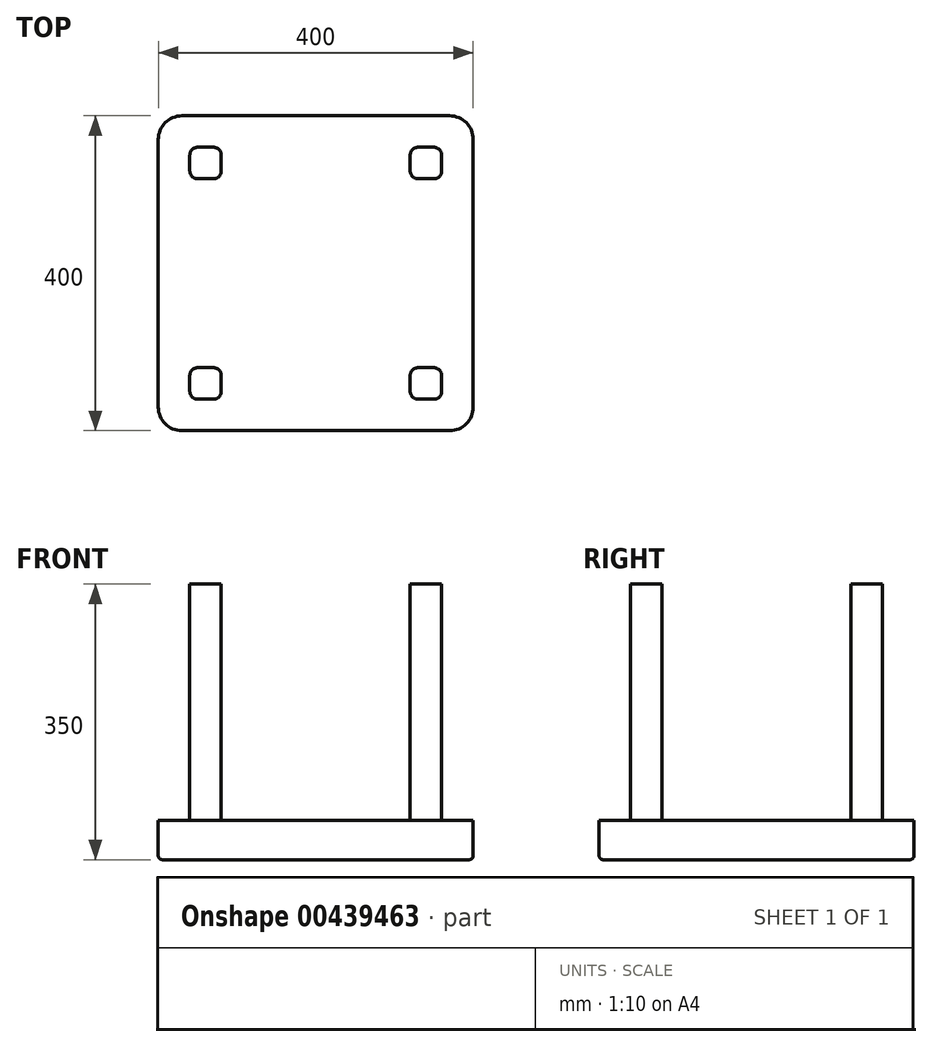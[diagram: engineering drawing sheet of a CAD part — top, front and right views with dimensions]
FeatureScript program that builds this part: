
annotation { "Feature Type Name" : "Feature", "Feature Type Description" : "" }
export const myFeature = defineFeature(function(context is Context, id is Id, definition is map)
    precondition{}
    {
        {
            var Q0;
            Q0=qCreatedBy(makeId("Top.planeOp"),FACE);
            var sketch = newSketch(context, id + "F0", { "sketchPlane" : qUnion([Q0])});
            skLineSegment(sketch, "E0.bottom", {"start": v(-186.1, 208.07) * mm, "end": v(153.9, 208.07) * mm});
            skLineSegment(sketch, "E0.top", {"start": v(-186.1, -191.93) * mm, "end": v(153.9, -191.93) * mm});
            skLineSegment(sketch, "E0.left", {"start": v(-216.1, 178.07) * mm, "end": v(-216.1, -161.93) * mm});
            skLineSegment(sketch, "E0.right", {"start": v(183.9, 178.07) * mm, "end": v(183.9, -161.93) * mm});
            skPoint(sketch, "E1.visualSharp", {"position": v(-216.1, 208.07) * mm});
            skArc(sketch, "E1.filletArc", {"start": v(-186.1, 208.07) * mm, "mid": v(-207.3, 199.28) * mm, "end": v(-216.1, 178.07) * mm});
            skPoint(sketch, "E2.visualSharp", {"position": v(183.9, 208.07) * mm});
            skArc(sketch, "E2.filletArc", {"start": v(183.9, 178.07) * mm, "mid": v(175.12, 199.28) * mm, "end": v(153.9, 208.07) * mm});
            skPoint(sketch, "E3.visualSharp", {"position": v(183.9, -191.93) * mm});
            skArc(sketch, "E3.filletArc", {"start": v(153.9, -191.93) * mm, "mid": v(175.12, -183.15) * mm, "end": v(183.9, -161.93) * mm});
            skPoint(sketch, "E4.visualSharp", {"position": v(-216.1, -191.93) * mm});
            skArc(sketch, "E4.filletArc", {"start": v(-216.1, -161.93) * mm, "mid": v(-207.3, -183.15) * mm, "end": v(-186.1, -191.93) * mm});
            skSolve(sketch);
        }
        {
            var Q0;
            Q0=makeQuery(id+"F0.imprint","IMPRINT",FACE,{"disambiguationData":[TD([[makeQuery(id+"F0.imprint","IMPRINT",EDGE,{"derivedFrom":sQuery(id+"F0.wireOp",EDGE,"E0.bottom")}),-1.0]])]});
            extrude(context, id + "F1", {"entities" : qUnion([Q0]), "depth" : 50 * mm});
        }
        {
            var Q0;
            Q0=qCreatedBy(makeId("Top.planeOp"),FACE);
            var sketch = newSketch(context, id + "F2", { "sketchPlane" : qUnion([Q0])});
            skLineSegment(sketch, "E5.bottom", {"start": v(133.9, -151.93) * mm, "end": v(113.9, -151.93) * mm});
            skLineSegment(sketch, "E5.top", {"start": v(133.9, -111.93) * mm, "end": v(113.9, -111.93) * mm});
            skLineSegment(sketch, "E5.left", {"start": v(143.9, -141.93) * mm, "end": v(143.9, -121.93) * mm});
            skLineSegment(sketch, "E5.right", {"start": v(103.9, -141.93) * mm, "end": v(103.9, -121.93) * mm});
            skLineSegment(sketch, "E6.bottom", {"start": v(133.9, 128.07) * mm, "end": v(113.9, 128.07) * mm});
            skLineSegment(sketch, "E6.top", {"start": v(133.9, 168.07) * mm, "end": v(113.9, 168.07) * mm});
            skLineSegment(sketch, "E6.left", {"start": v(143.9, 138.07) * mm, "end": v(143.9, 158.07) * mm});
            skLineSegment(sketch, "E6.right", {"start": v(103.9, 138.07) * mm, "end": v(103.9, 158.07) * mm});
            skLineSegment(sketch, "E7.bottom", {"start": v(-146.1, -151.93) * mm, "end": v(-166.1, -151.93) * mm});
            skLineSegment(sketch, "E7.top", {"start": v(-146.1, -111.93) * mm, "end": v(-166.1, -111.93) * mm});
            skLineSegment(sketch, "E7.left", {"start": v(-136.1, -141.93) * mm, "end": v(-136.1, -121.93) * mm});
            skLineSegment(sketch, "E7.right", {"start": v(-176.1, -141.93) * mm, "end": v(-176.1, -121.93) * mm});
            skLineSegment(sketch, "E8.bottom", {"start": v(-146.1, 128.07) * mm, "end": v(-166.1, 128.07) * mm});
            skLineSegment(sketch, "E8.top", {"start": v(-146.1, 168.07) * mm, "end": v(-166.1, 168.07) * mm});
            skLineSegment(sketch, "E8.left", {"start": v(-136.1, 138.07) * mm, "end": v(-136.1, 158.07) * mm});
            skLineSegment(sketch, "E8.right", {"start": v(-176.1, 138.07) * mm, "end": v(-176.1, 158.07) * mm});
            skPoint(sketch, "E9.visualSharp", {"position": v(-176.1, -151.93) * mm});
            skArc(sketch, "E9.filletArc", {"start": v(-176.1, -141.93) * mm, "mid": v(-173.16, -149) * mm, "end": v(-166.1, -151.93) * mm});
            skPoint(sketch, "E10.visualSharp", {"position": v(-176.1, -111.93) * mm});
            skArc(sketch, "E10.filletArc", {"start": v(-166.1, -111.93) * mm, "mid": v(-173.16, -114.86) * mm, "end": v(-176.1, -121.93) * mm});
            skPoint(sketch, "E11.visualSharp", {"position": v(-136.1, -111.93) * mm});
            skArc(sketch, "E11.filletArc", {"start": v(-136.1, -121.93) * mm, "mid": v(-139.02, -114.86) * mm, "end": v(-146.1, -111.93) * mm});
            skPoint(sketch, "E12.visualSharp", {"position": v(-136.1, -151.93) * mm});
            skArc(sketch, "E12.filletArc", {"start": v(-146.1, -151.93) * mm, "mid": v(-139.02, -149) * mm, "end": v(-136.1, -141.93) * mm});
            skPoint(sketch, "E13.visualSharp", {"position": v(-176.1, 128.07) * mm});
            skArc(sketch, "E13.filletArc", {"start": v(-176.1, 138.07) * mm, "mid": v(-173.16, 131) * mm, "end": v(-166.1, 128.07) * mm});
            skPoint(sketch, "E14.visualSharp", {"position": v(-176.1, 168.07) * mm});
            skArc(sketch, "E14.filletArc", {"start": v(-166.1, 168.07) * mm, "mid": v(-173.16, 165.14) * mm, "end": v(-176.1, 158.07) * mm});
            skPoint(sketch, "E15.visualSharp", {"position": v(-136.1, 168.07) * mm});
            skArc(sketch, "E15.filletArc", {"start": v(-136.1, 158.07) * mm, "mid": v(-139.02, 165.14) * mm, "end": v(-146.1, 168.07) * mm});
            skPoint(sketch, "E16.visualSharp", {"position": v(-136.1, 128.07) * mm});
            skArc(sketch, "E16.filletArc", {"start": v(-146.1, 128.07) * mm, "mid": v(-139.02, 131) * mm, "end": v(-136.1, 138.07) * mm});
            skPoint(sketch, "E17.visualSharp", {"position": v(103.9, 128.07) * mm});
            skArc(sketch, "E17.filletArc", {"start": v(103.9, 138.07) * mm, "mid": v(106.84, 131) * mm, "end": v(113.9, 128.07) * mm});
            skPoint(sketch, "E18.visualSharp", {"position": v(103.9, 168.07) * mm});
            skArc(sketch, "E18.filletArc", {"start": v(113.9, 168.07) * mm, "mid": v(106.84, 165.14) * mm, "end": v(103.9, 158.07) * mm});
            skPoint(sketch, "E19.visualSharp", {"position": v(143.9, 168.07) * mm});
            skArc(sketch, "E19.filletArc", {"start": v(143.9, 158.07) * mm, "mid": v(140.98, 165.14) * mm, "end": v(133.9, 168.07) * mm});
            skPoint(sketch, "E20.visualSharp", {"position": v(143.9, 128.07) * mm});
            skArc(sketch, "E20.filletArc", {"start": v(133.9, 128.07) * mm, "mid": v(140.98, 131) * mm, "end": v(143.9, 138.07) * mm});
            skPoint(sketch, "E21.visualSharp", {"position": v(143.9, -111.93) * mm});
            skArc(sketch, "E21.filletArc", {"start": v(143.9, -121.93) * mm, "mid": v(140.98, -114.86) * mm, "end": v(133.9, -111.93) * mm});
            skPoint(sketch, "E22.visualSharp", {"position": v(103.9, -111.93) * mm});
            skArc(sketch, "E22.filletArc", {"start": v(113.9, -111.93) * mm, "mid": v(106.84, -114.86) * mm, "end": v(103.9, -121.93) * mm});
            skPoint(sketch, "E23.visualSharp", {"position": v(103.9, -151.93) * mm});
            skArc(sketch, "E23.filletArc", {"start": v(103.9, -141.93) * mm, "mid": v(106.84, -149) * mm, "end": v(113.9, -151.93) * mm});
            skPoint(sketch, "E24.visualSharp", {"position": v(143.9, -151.93) * mm});
            skArc(sketch, "E24.filletArc", {"start": v(133.9, -151.93) * mm, "mid": v(140.98, -149) * mm, "end": v(143.9, -141.93) * mm});
            skSolve(sketch);
        }
        {
            var Q0;
            Q0=makeQuery(id+"F2.imprint","IMPRINT",FACE,{"disambiguationData":[TD([[makeQuery(id+"F2.imprint","IMPRINT",EDGE,{"derivedFrom":sQuery(id+"F2.wireOp",EDGE,"E5.bottom")}),-1.0]])]});
            var Q1;
            Q1=makeQuery(id+"F2.imprint","IMPRINT",FACE,{"disambiguationData":[TD([[makeQuery(id+"F2.imprint","IMPRINT",EDGE,{"derivedFrom":sQuery(id+"F2.wireOp",EDGE,"E6.bottom")}),-1.0]])]});
            var Q2;
            Q2=makeQuery(id+"F2.imprint","IMPRINT",FACE,{"disambiguationData":[TD([[makeQuery(id+"F2.imprint","IMPRINT",EDGE,{"derivedFrom":sQuery(id+"F2.wireOp",EDGE,"E8.bottom")}),-1.0]])]});
            var Q3;
            Q3=makeQuery(id+"F2.imprint","IMPRINT",FACE,{"disambiguationData":[TD([[makeQuery(id+"F2.imprint","IMPRINT",EDGE,{"derivedFrom":sQuery(id+"F2.wireOp",EDGE,"E7.bottom")}),-1.0]])]});
            extrude(context, id + "F3", {"entities" : qUnion([Q0, Q1, Q2, Q3]), "operationType" : NewBodyOperationType.ADD, "depth" : 350 * mm});
        }
        {
            var Q0;
            Q0=makeQuery(id+"F1.opExtrude","CAP_EDGE",EDGE,{"disambiguationData":[OSD([sQuery(id+"F0.wireOp",EDGE,"E0.bottom")])],"isStart":true});
            fillet(context, id + "F4", {"entities" : qUnion([Q0]), "radius" : 5 * mm, "tangentPropagation" : true, "allowEdgeOverflow" : false});
        }
    });
